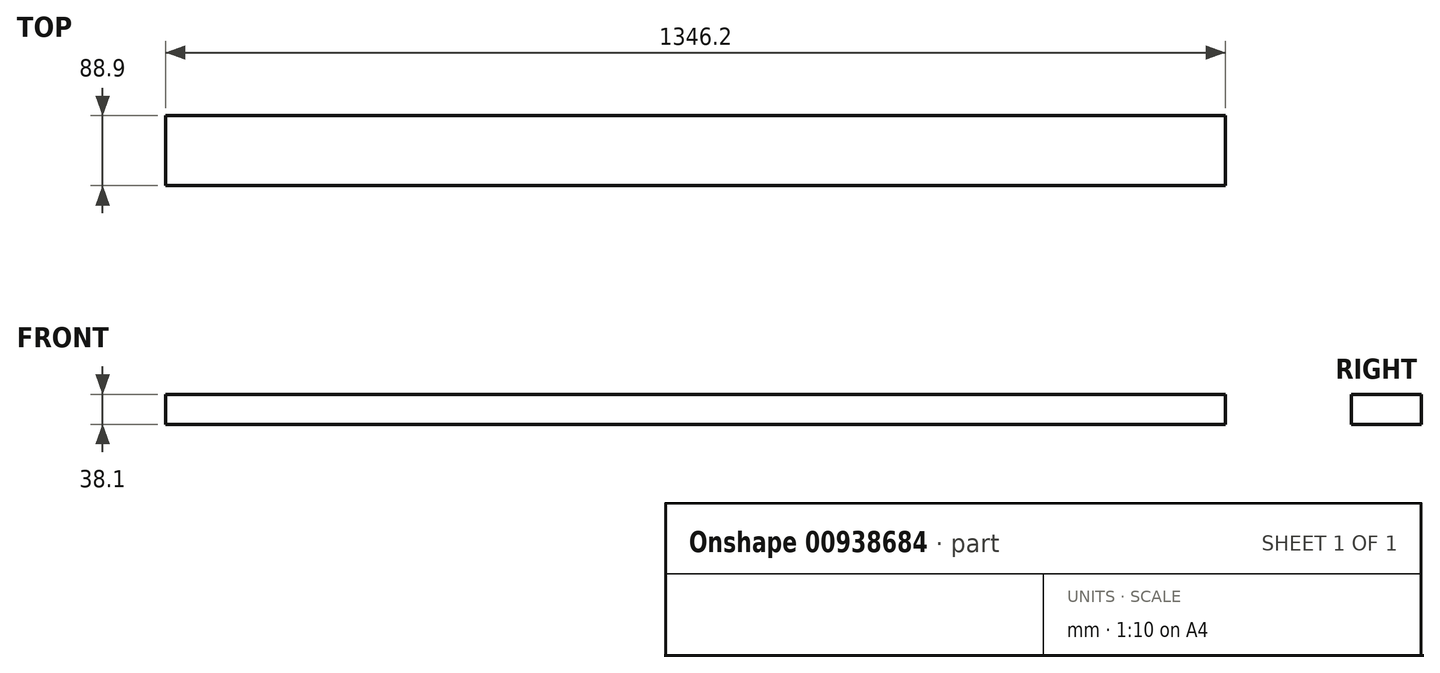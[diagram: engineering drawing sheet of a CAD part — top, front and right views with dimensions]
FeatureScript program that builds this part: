
annotation { "Feature Type Name" : "Feature", "Feature Type Description" : "" }
export const myFeature = defineFeature(function(context is Context, id is Id, definition is map)
    precondition{}
    {
        {
            var Q0;
            Q0=qCreatedBy(makeId("Right.planeOp"),FACE);
            var sketch = newSketch(context, id + "F0", { "sketchPlane" : qUnion([Q0])});
            skLineSegment(sketch, "E0.bottom", {"start": v(44.45, -19.05) * mm, "end": v(-44.45, -19.05) * mm});
            skLineSegment(sketch, "E0.top", {"start": v(44.45, 19.05) * mm, "end": v(-44.45, 19.05) * mm});
            skLineSegment(sketch, "E0.left", {"start": v(44.45, -19.05) * mm, "end": v(44.45, 19.05) * mm});
            skLineSegment(sketch, "E0.right", {"start": v(-44.45, -19.05) * mm, "end": v(-44.45, 19.05) * mm});
            skPoint(sketch, "E0.middle", {"position": v(0, 0) * mm});
            skSolve(sketch);
        }
        {
            var Q0;
            Q0=qSketchRegion(id+"F0",true);
            var Q1;
            Q1=makeQuery(id+"F0.imprint","IMPRINT",FACE,{"disambiguationData":[TD([[makeQuery(id+"F0.imprint","IMPRINT",EDGE,{"derivedFrom":sQuery(id+"F0.wireOp",EDGE,"E0.bottom")}),-1.0]])]});
            extrude(context, id + "F1", {"entities" : qUnion([Q0, Q1]), "depth" : 1346.2 * mm, "offsetDistance" : 25.4 * mm});
        }
    });
